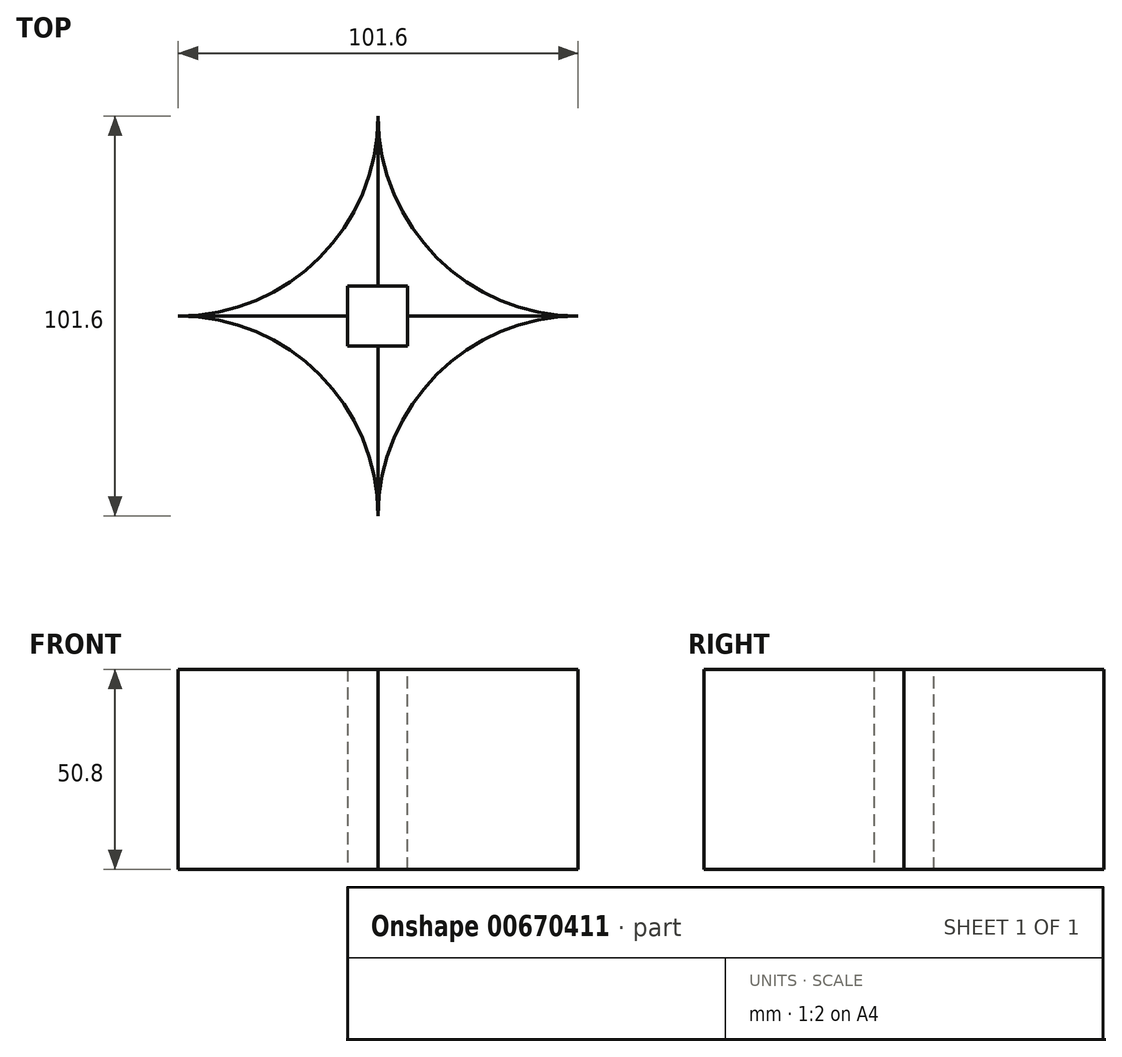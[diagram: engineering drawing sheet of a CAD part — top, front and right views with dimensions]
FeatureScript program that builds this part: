
annotation { "Feature Type Name" : "Feature", "Feature Type Description" : "" }
export const myFeature = defineFeature(function(context is Context, id is Id, definition is map)
    precondition{}
    {
        {
            var Q0;
            Q0=qCreatedBy(makeId("Top.planeOp"),FACE);
            var sketch = newSketch(context, id + "F0", { "sketchPlane" : qUnion([Q0])});
            skLineSegment(sketch, "E0.bottom", {"start": v(-50.65, 0) * mm, "end": v(0.15, 0) * mm});
            skLineSegment(sketch, "E0.right", {"start": v(0.15, 0) * mm, "end": v(0.15, 50.8) * mm});
            skArc(sketch, "E1", {"start": v(-50.65, 0) * mm, "mid": v(-14.72, 14.88) * mm, "end": v(0.15, 50.8) * mm});
            skSolve(sketch);
        }
        {
            var Q0;
            Q0=qCreatedBy(makeId("Top.planeOp"),FACE);
            var sketch = newSketch(context, id + "F1", { "sketchPlane" : qUnion([Q0])});
            skLineSegment(sketch, "E2.bottom", {"start": v(-7.62, -7.62) * mm, "end": v(7.62, -7.62) * mm});
            skLineSegment(sketch, "E2.top", {"start": v(-7.62, 7.62) * mm, "end": v(7.62, 7.62) * mm});
            skLineSegment(sketch, "E2.left", {"start": v(-7.62, -7.62) * mm, "end": v(-7.62, 7.62) * mm});
            skLineSegment(sketch, "E2.right", {"start": v(7.62, -7.62) * mm, "end": v(7.62, 7.62) * mm});
            skSolve(sketch);
        }
        {
            var Q0;
            Q0=makeQuery(id+"F0.imprint","IMPRINT",FACE,{"disambiguationData":[TD([[makeQuery(id+"F0.imprint","IMPRINT",EDGE,{"derivedFrom":sQuery(id+"F0.wireOp",EDGE,"E0.bottom")}),1.0]])]});
            extrude(context, id + "F2", {"entities" : qUnion([Q0]), "depth" : 50.8 * mm, "offsetDistance" : 25.4 * mm});
        }
        {
            var Q0;
            Q0=makeQuery(id+"F2.opExtrude","SWEPT_BODY",BODY,{"disambiguationData":[OSD([sQuery(id+"F0.wireOp",EDGE,"E0.bottom"),sQuery(id+"F0.wireOp",EDGE,"E0.right"),sQuery(id+"F0.wireOp",EDGE,"E1")])]});
            var Q1;
            Q1=makeQuery(id+"F2.opExtrude","SWEPT_EDGE",EDGE,{"disambiguationData":[OSD([sQuery(id+"F0.wireOp",EDGE,"E0.bottom"),sQuery(id+"F0.wireOp",EDGE,"E0.right")])]});
            circularPattern(context, id + "F3", {"entities" : qUnion([Q0]), "axis" : qUnion([Q1]), "angle" : 360 * degree, "instanceCount" : 4, "equalSpace" : true});
        }
        {
            var Q0;
            Q0=makeQuery(id+"F1.imprint","IMPRINT",FACE,{"disambiguationData":[TD([[makeQuery(id+"F1.imprint","IMPRINT",EDGE,{"derivedFrom":sQuery(id+"F1.wireOp",EDGE,"E2.bottom")}),1.0]])]});
            extrude(context, id + "F4", {"entities" : qUnion([Q0]), "operationType" : NewBodyOperationType.REMOVE, "endBound" : BoundingType.THROUGH_ALL, "depth" : 25.4 * mm, "offsetDistance" : 25.4 * mm});
        }
    });
